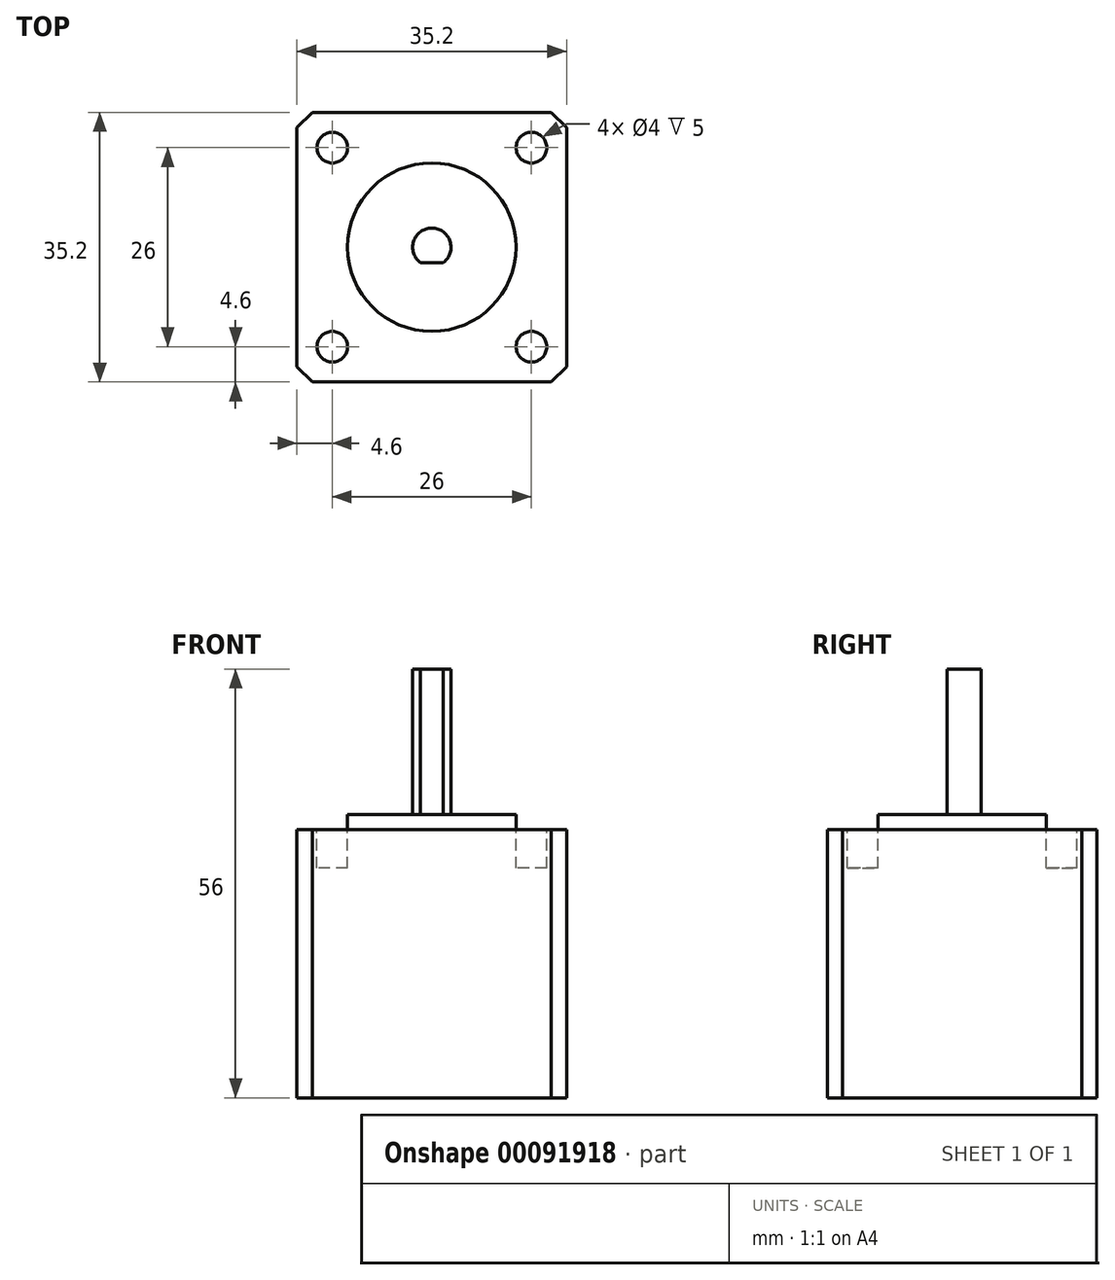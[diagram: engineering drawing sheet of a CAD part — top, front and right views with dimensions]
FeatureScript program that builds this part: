
annotation { "Feature Type Name" : "Feature", "Feature Type Description" : "" }
export const myFeature = defineFeature(function(context is Context, id is Id, definition is map)
    precondition{}
    {
        {
            var Q0;
            Q0=qCreatedBy(makeId("Top.planeOp"),FACE);
            var sketch = newSketch(context, id + "F0", { "sketchPlane" : qUnion([Q0])});
            skLineSegment(sketch, "E0.bottom", {"start": v(17.6, 17.6) * mm, "end": v(-17.6, 17.6) * mm});
            skLineSegment(sketch, "E0.top", {"start": v(17.6, -17.6) * mm, "end": v(-17.6, -17.6) * mm});
            skLineSegment(sketch, "E0.left", {"start": v(17.6, 17.6) * mm, "end": v(17.6, -17.6) * mm});
            skLineSegment(sketch, "E0.right", {"start": v(-17.6, 17.6) * mm, "end": v(-17.6, -17.6) * mm});
            skPoint(sketch, "E0.middle", {"position": v(0, 0) * mm});
            skSolve(sketch);
        }
        {
            var Q0;
            Q0=makeQuery(id+"F0.imprint","IMPRINT",FACE,{"disambiguationData":[TD([[makeQuery(id+"F0.imprint","IMPRINT",EDGE,{"derivedFrom":sQuery(id+"F0.wireOp",EDGE,"E0.bottom")}),1.0]])]});
            extrude(context, id + "F1", {"entities" : qUnion([Q0]), "depth" : 35 * mm, "symmetric" : true});
        }
        {
            var Q0;
            Q0=makeQuery(id+"F1.opExtrude","SWEPT_EDGE",EDGE,{"disambiguationData":[OSD([sQuery(id+"F0.wireOp",EDGE,"E0.bottom"),sQuery(id+"F0.wireOp",EDGE,"E0.right")])]});
            var Q1;
            Q1=makeQuery(id+"F1.opExtrude","SWEPT_EDGE",EDGE,{"disambiguationData":[OSD([sQuery(id+"F0.wireOp",EDGE,"E0.top"),sQuery(id+"F0.wireOp",EDGE,"E0.right")])]});
            var Q2;
            Q2=makeQuery(id+"F1.opExtrude","SWEPT_EDGE",EDGE,{"disambiguationData":[OSD([sQuery(id+"F0.wireOp",EDGE,"E0.top"),sQuery(id+"F0.wireOp",EDGE,"E0.left")])]});
            var Q3;
            Q3=makeQuery(id+"F1.opExtrude","SWEPT_EDGE",EDGE,{"disambiguationData":[OSD([sQuery(id+"F0.wireOp",EDGE,"E0.bottom"),sQuery(id+"F0.wireOp",EDGE,"E0.left")])]});
            chamfer(context, id + "F2", {"entities" : qUnion([Q0, Q1, Q2, Q3]), "width" : 2 * mm, "tangentPropagation" : true});
        }
        {
            var Q0;
            Q0=makeQuery(id+"F1.opExtrude","CAP_FACE",FACE,{"disambiguationData":[OSD([sQuery(id+"F0.wireOp",EDGE,"E0.bottom"),sQuery(id+"F0.wireOp",EDGE,"E0.top"),sQuery(id+"F0.wireOp",EDGE,"E0.left"),sQuery(id+"F0.wireOp",EDGE,"E0.right")])],"isStart":false});
            var sketch = newSketch(context, id + "F3", { "sketchPlane" : qUnion([Q0])});
            skCircle(sketch, "E1", {"center": v(0, 0) * mm, "radius": 11 * mm});
            skSolve(sketch);
        }
        {
            var Q0;
            Q0=makeQuery(id+"F3.imprint","IMPRINT",FACE,{"disambiguationData":[TD([[makeQuery(id+"F3.imprint","IMPRINT",EDGE,{"derivedFrom":sQuery(id+"F3.wireOp",EDGE,"E1")}),1.0]])]});
            extrude(context, id + "F4", {"entities" : qUnion([Q0]), "operationType" : NewBodyOperationType.ADD, "depth" : 2 * mm});
        }
        {
            var Q0;
            Q0=makeQuery(id+"F1.opExtrude","CAP_FACE",FACE,{"disambiguationData":[OSD([sQuery(id+"F0.wireOp",EDGE,"E0.bottom"),sQuery(id+"F0.wireOp",EDGE,"E0.top"),sQuery(id+"F0.wireOp",EDGE,"E0.left"),sQuery(id+"F0.wireOp",EDGE,"E0.right")])],"isStart":false});
            var sketch = newSketch(context, id + "F5", { "sketchPlane" : qUnion([Q0])});
            skCircle(sketch, "E2", {"center": v(-13, 13) * mm, "radius": 2 * mm});
            skCircle(sketch, "E3.MirrorC", {"center": v(13, 13) * mm, "radius": 2 * mm});
            skCircle(sketch, "E4.MirrorC", {"center": v(-13, -13) * mm, "radius": 2 * mm});
            skCircle(sketch, "E5.MirrorC", {"center": v(13, -13) * mm, "radius": 2 * mm});
            skSolve(sketch);
        }
        {
            var Q0;
            Q0 = qSketchRegion(id + "F5", true);
            extrude(context, id + "F6", {"entities" : qUnion([Q0]), "operationType" : NewBodyOperationType.REMOVE, "oppositeDirection" : true, "depth" : 5 * mm});
        }
        {
            var Q0;
            Q0=makeQuery(id+"F4.opExtrude","CAP_FACE",FACE,{"disambiguationData":[OSD([sQuery(id+"F3.wireOp",EDGE,"E1")])],"isStart":false});
            var sketch = newSketch(context, id + "F7", { "sketchPlane" : qUnion([Q0])});
            skCircle(sketch, "E6", {"center": v(0, 0) * mm, "radius": 2.5 * mm});
            skSolve(sketch);
        }
        {
            var Q0;
            Q0 = qSketchRegion(id + "F7", true);
            extrude(context, id + "F8", {"entities" : qUnion([Q0]), "operationType" : NewBodyOperationType.ADD, "depth" : 19 * mm});
        }
        {
            var Q0;
            Q0=qCreatedBy(makeId("Front.planeOp"),FACE);
            cPlane(context, id + "F9", {"entities" : qUnion([Q0]), "cplaneType" : CPlaneType.OFFSET, "offset" : 2 * mm, "width" : 150 * mm, "height" : 150 * mm});
        }
        {
            var Q0;
            Q0=qCreatedBy(id+"F9.planeOp",FACE);
            var sketch = newSketch(context, id + "F10", { "sketchPlane" : qUnion([Q0])});
            skLineSegment(sketch, "E7.bottom", {"start": v(2.5, 38.5) * mm, "end": v(-2.5, 38.5) * mm});
            skLineSegment(sketch, "E7.top", {"start": v(2.5, 19.5) * mm, "end": v(-2.5, 19.5) * mm});
            skLineSegment(sketch, "E7.left", {"start": v(2.5, 38.5) * mm, "end": v(2.5, 19.5) * mm});
            skLineSegment(sketch, "E7.right", {"start": v(-2.5, 38.5) * mm, "end": v(-2.5, 19.5) * mm});
            skPoint(sketch, "E7.middle", {"position": v(0, 29) * mm});
            skSolve(sketch);
        }
        {
            var Q0;
            Q0 = qSketchRegion(id + "F10", true);
            extrude(context, id + "F11", {"entities" : qUnion([Q0]), "operationType" : NewBodyOperationType.REMOVE, "endBound" : BoundingType.THROUGH_ALL, "depth" : 25 * mm});
        }
    });
